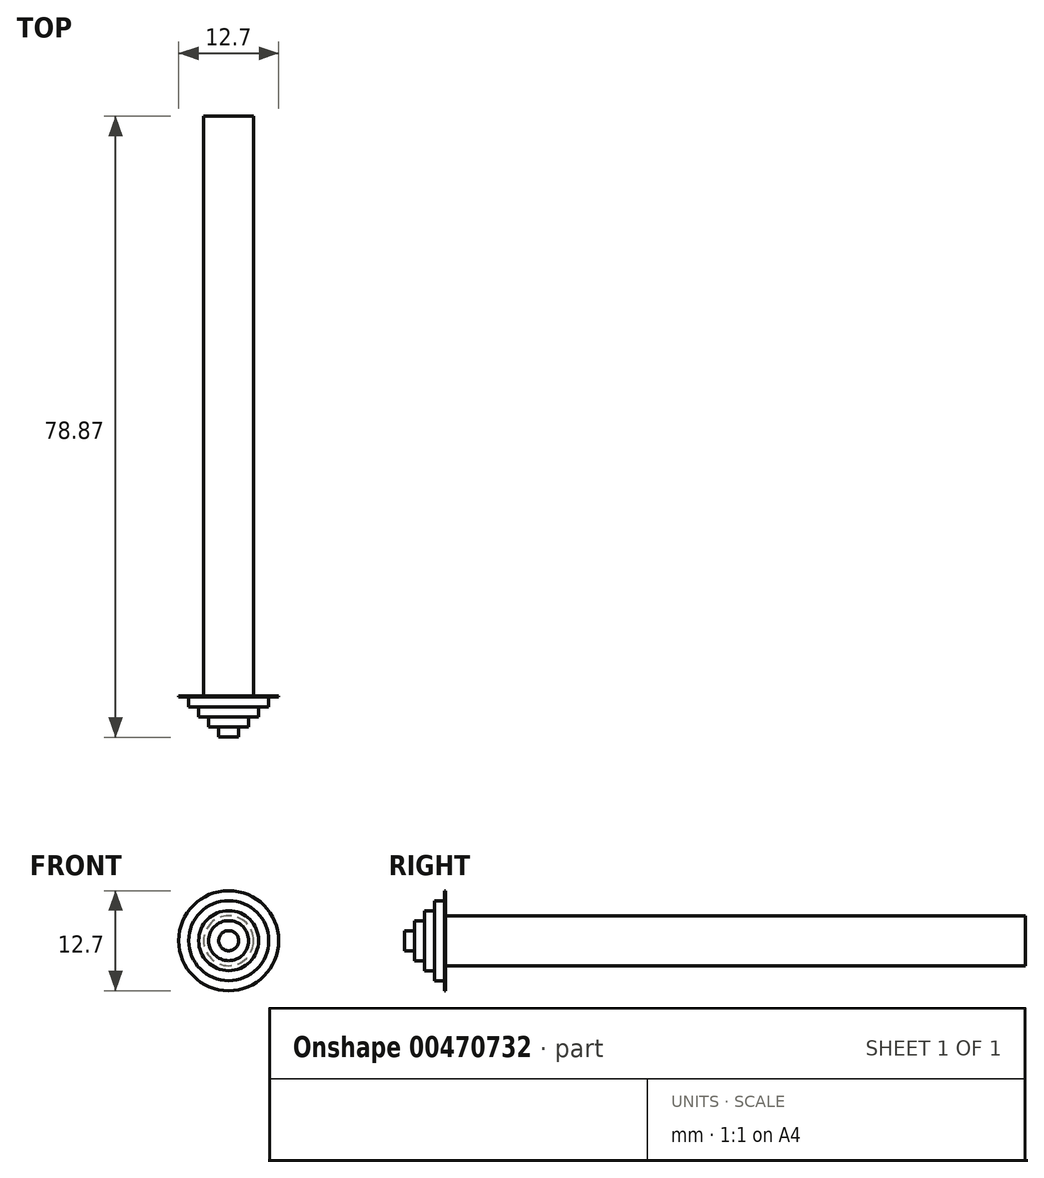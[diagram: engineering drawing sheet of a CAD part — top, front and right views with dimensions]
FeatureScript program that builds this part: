
annotation { "Feature Type Name" : "Feature", "Feature Type Description" : "" }
export const myFeature = defineFeature(function(context is Context, id is Id, definition is map)
    precondition{}
    {
        {
            var Q0;
            Q0=qCreatedBy(makeId("Front.planeOp"),FACE);
            var sketch = newSketch(context, id + "F0", { "sketchPlane" : qUnion([Q0])});
            skCircle(sketch, "E0", {"center": v(0, 0) * mm, "radius": 6.35 * mm});
            skSolve(sketch);
        }
        {
            var Q0;
            Q0 = qSketchRegion(id + "F0", true);
            extrude(context, id + "F1", {"entities" : qUnion([Q0]), "depth" : 0.13 * mm});
        }
        {
            var Q0;
            Q0=makeQuery(id+"F1.opExtrude","CAP_FACE",FACE,{"disambiguationData":[OSD([sQuery(id+"F0.wireOp",EDGE,"E0")])],"isStart":false});
            var sketch = newSketch(context, id + "F2", { "sketchPlane" : qUnion([Q0])});
            skCircle(sketch, "E1", {"center": v(0, 0) * mm, "radius": 5.08 * mm});
            skSolve(sketch);
        }
        {
            var Q0;
            Q0=makeQuery(id+"F2.imprint","IMPRINT",FACE,{"disambiguationData":[TD([[makeQuery(id+"F2.imprint","IMPRINT",EDGE,{"derivedFrom":sQuery(id+"F2.wireOp",EDGE,"E1")}),1.0]])]});
            var sketch = newSketch(context, id + "F3", { "sketchPlane" : qUnion([Q0])});
            skCircle(sketch, "E2", {"center": v(0, 0) * mm, "radius": 3.8 * mm});
            skCircle(sketch, "E3", {"center": v(0, 0) * mm, "radius": 2.54 * mm});
            skCircle(sketch, "E4", {"center": v(0, 0) * mm, "radius": 1.27 * mm});
            skSolve(sketch);
        }
        {
            var Q0;
            Q0=makeQuery(id+"F3.imprint","IMPRINT",FACE,{"disambiguationData":[TD([[makeQuery(id+"F3.imprint","IMPRINT",EDGE,{"derivedFrom":sQuery(id+"F3.wireOp",EDGE,"E2")}),-1.0]])]});
            extrude(context, id + "F4", {"entities" : qUnion([Q0]), "operationType" : NewBodyOperationType.ADD, "depth" : 1.27 * mm});
        }
        {
            var Q0;
            Q0 = qSketchRegion(id + "F3", true);
            extrude(context, id + "F5", {"entities" : qUnion([Q0]), "operationType" : NewBodyOperationType.ADD, "depth" : 2.54 * mm});
        }
        {
            var Q0;
            Q0=makeQuery(id+"F3.imprint","IMPRINT",FACE,{"disambiguationData":[TD([[makeQuery(id+"F3.imprint","IMPRINT",EDGE,{"derivedFrom":sQuery(id+"F3.wireOp",EDGE,"E3")}),1.0]])]});
            extrude(context, id + "F6", {"entities" : qUnion([Q0]), "operationType" : NewBodyOperationType.ADD, "depth" : 3.8 * mm});
        }
        {
            var Q0;
            Q0=makeQuery(id+"F3.imprint","IMPRINT",FACE,{"disambiguationData":[TD([[makeQuery(id+"F3.imprint","IMPRINT",EDGE,{"derivedFrom":sQuery(id+"F3.wireOp",EDGE,"E4")}),1.0]])]});
            extrude(context, id + "F7", {"entities" : qUnion([Q0]), "operationType" : NewBodyOperationType.ADD, "depth" : 5.08 * mm});
        }
        {
            var Q0;
            Q0=makeQuery(id+"F0.imprint","IMPRINT",FACE,{"disambiguationData":[TD([[makeQuery(id+"F0.imprint","IMPRINT",EDGE,{"derivedFrom":sQuery(id+"F0.wireOp",EDGE,"E0")}),1.0]])]});
            var sketch = newSketch(context, id + "F8", { "sketchPlane" : qUnion([Q0])});
            skCircle(sketch, "E5", {"center": v(0, 0) * mm, "radius": 3.18 * mm});
            skSolve(sketch);
        }
        {
            var Q0;
            Q0=makeQuery(id+"F8.imprint","IMPRINT",FACE,{"disambiguationData":[TD([[makeQuery(id+"F8.imprint","IMPRINT",EDGE,{"derivedFrom":sQuery(id+"F8.wireOp",EDGE,"E5")}),1.0]])]});
            extrude(context, id + "F9", {"entities" : qUnion([Q0]), "operationType" : NewBodyOperationType.ADD, "oppositeDirection" : true, "depth" : 73.66 * mm});
        }
    });
